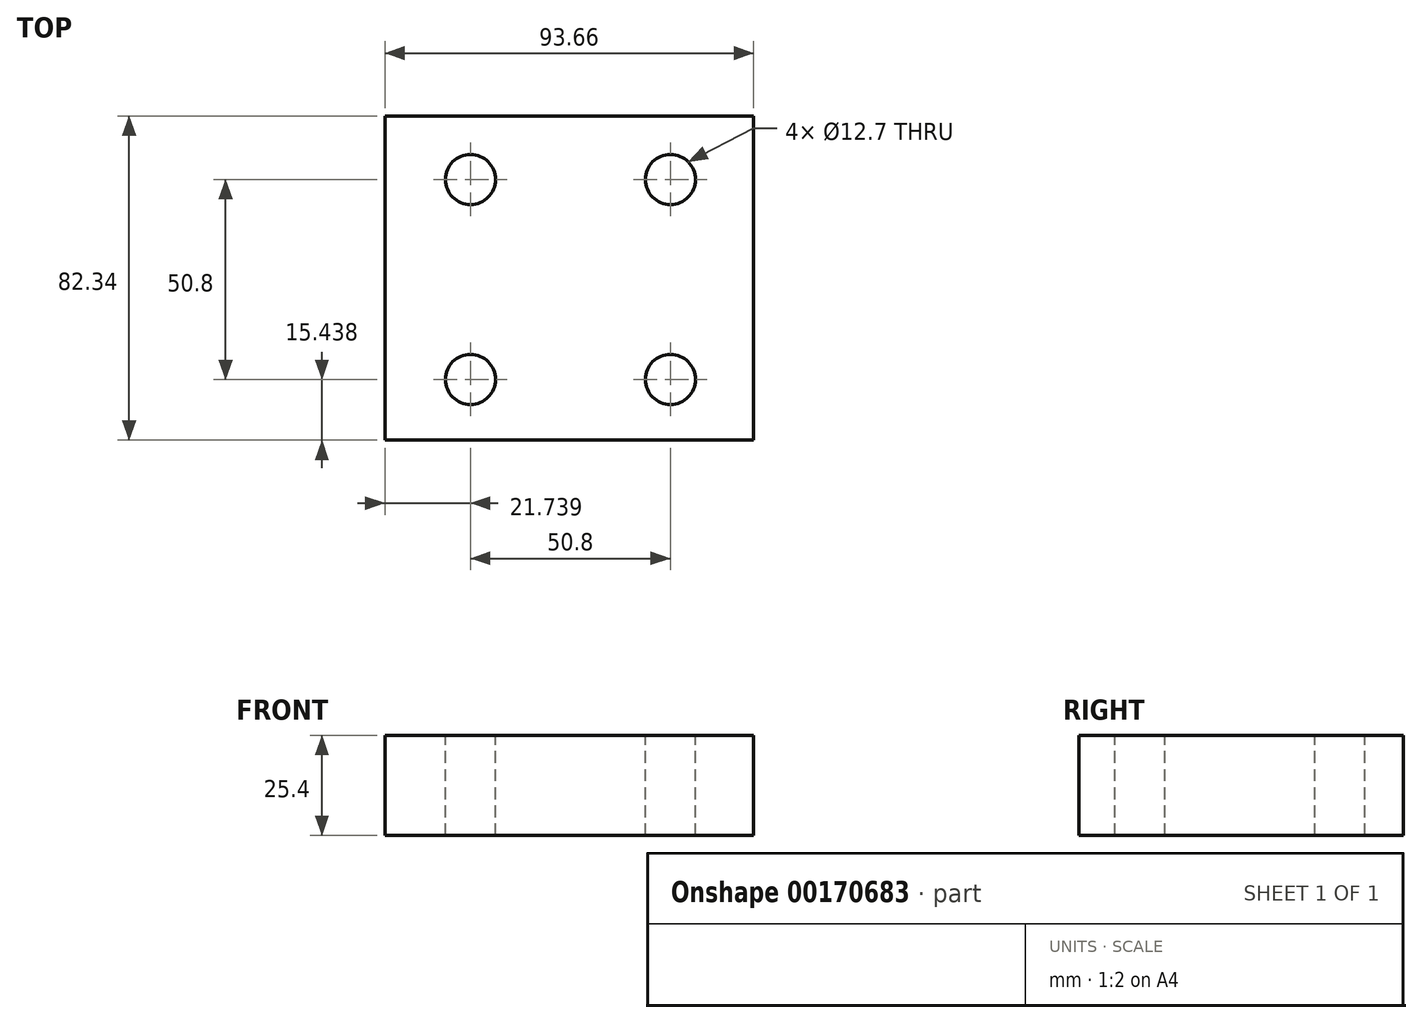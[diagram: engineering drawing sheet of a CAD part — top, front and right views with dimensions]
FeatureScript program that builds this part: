
annotation { "Feature Type Name" : "Feature", "Feature Type Description" : "" }
export const myFeature = defineFeature(function(context is Context, id is Id, definition is map)
    precondition{}
    {
        {
            var Q0;
            Q0=qCreatedBy(makeId("Top.planeOp"),FACE);
            var sketch = newSketch(context, id + "F0", { "sketchPlane" : qUnion([Q0])});
            skLineSegment(sketch, "E0.bottom", {"start": v(-46.16, 0) * mm, "end": v(47.5, 0) * mm});
            skLineSegment(sketch, "E0.top", {"start": v(-46.16, 82.34) * mm, "end": v(47.5, 82.34) * mm});
            skLineSegment(sketch, "E0.left", {"start": v(-46.16, 0) * mm, "end": v(-46.16, 82.34) * mm});
            skLineSegment(sketch, "E0.right", {"start": v(47.5, 0) * mm, "end": v(47.5, 82.34) * mm});
            skSolve(sketch);
        }
        {
            var Q0;
            Q0=makeQuery(id+"F0.imprint","IMPRINT",FACE,{"disambiguationData":[TD([[makeQuery(id+"F0.imprint","IMPRINT",EDGE,{"derivedFrom":sQuery(id+"F0.wireOp",EDGE,"E0.bottom")}),1.0]])]});
            extrude(context, id + "F2", {"entities" : qUnion([Q0]), "depth" : 25.4 * mm});
        }
        {
            var Q0;
            Q0=makeQuery(id+"F2.opExtrude","CAP_FACE",FACE,{"disambiguationData":[OSD([sQuery(id+"F0.wireOp",EDGE,"E0.bottom"),sQuery(id+"F0.wireOp",EDGE,"E0.top"),sQuery(id+"F0.wireOp",EDGE,"E0.left"),sQuery(id+"F0.wireOp",EDGE,"E0.right")])],"isStart":false});
            var sketch = newSketch(context, id + "F3", { "sketchPlane" : qUnion([Q0])});
            skCircle(sketch, "E1", {"center": v(26.38, 66.24) * mm, "radius": 6.35 * mm});
            skCircle(sketch, "E2", {"center": v(26.38, 15.44) * mm, "radius": 6.35 * mm});
            skCircle(sketch, "E3", {"center": v(-24.42, 66.24) * mm, "radius": 6.35 * mm});
            skCircle(sketch, "E4", {"center": v(-24.42, 15.44) * mm, "radius": 6.35 * mm});
            skLineSegment(sketch, "E5.bottom", {"start": v(26.38, 15.44) * mm, "end": v(-24.42, 15.44) * mm, "construction": true});
            skLineSegment(sketch, "E5.top", {"start": v(26.38, 66.24) * mm, "end": v(-24.42, 66.24) * mm, "construction": true});
            skLineSegment(sketch, "E5.left", {"start": v(26.38, 15.44) * mm, "end": v(26.38, 66.24) * mm, "construction": true});
            skLineSegment(sketch, "E5.right", {"start": v(-24.42, 15.44) * mm, "end": v(-24.42, 66.24) * mm, "construction": true});
            skSolve(sketch);
        }
        {
            var Q0;
            Q0 = qSketchRegion(id + "F3", true);
            extrude(context, id + "F1", {"entities" : qUnion([Q0]), "operationType" : NewBodyOperationType.REMOVE, "endBound" : BoundingType.THROUGH_ALL, "oppositeDirection" : true, "depth" : 25.4 * mm});
        }
    });
